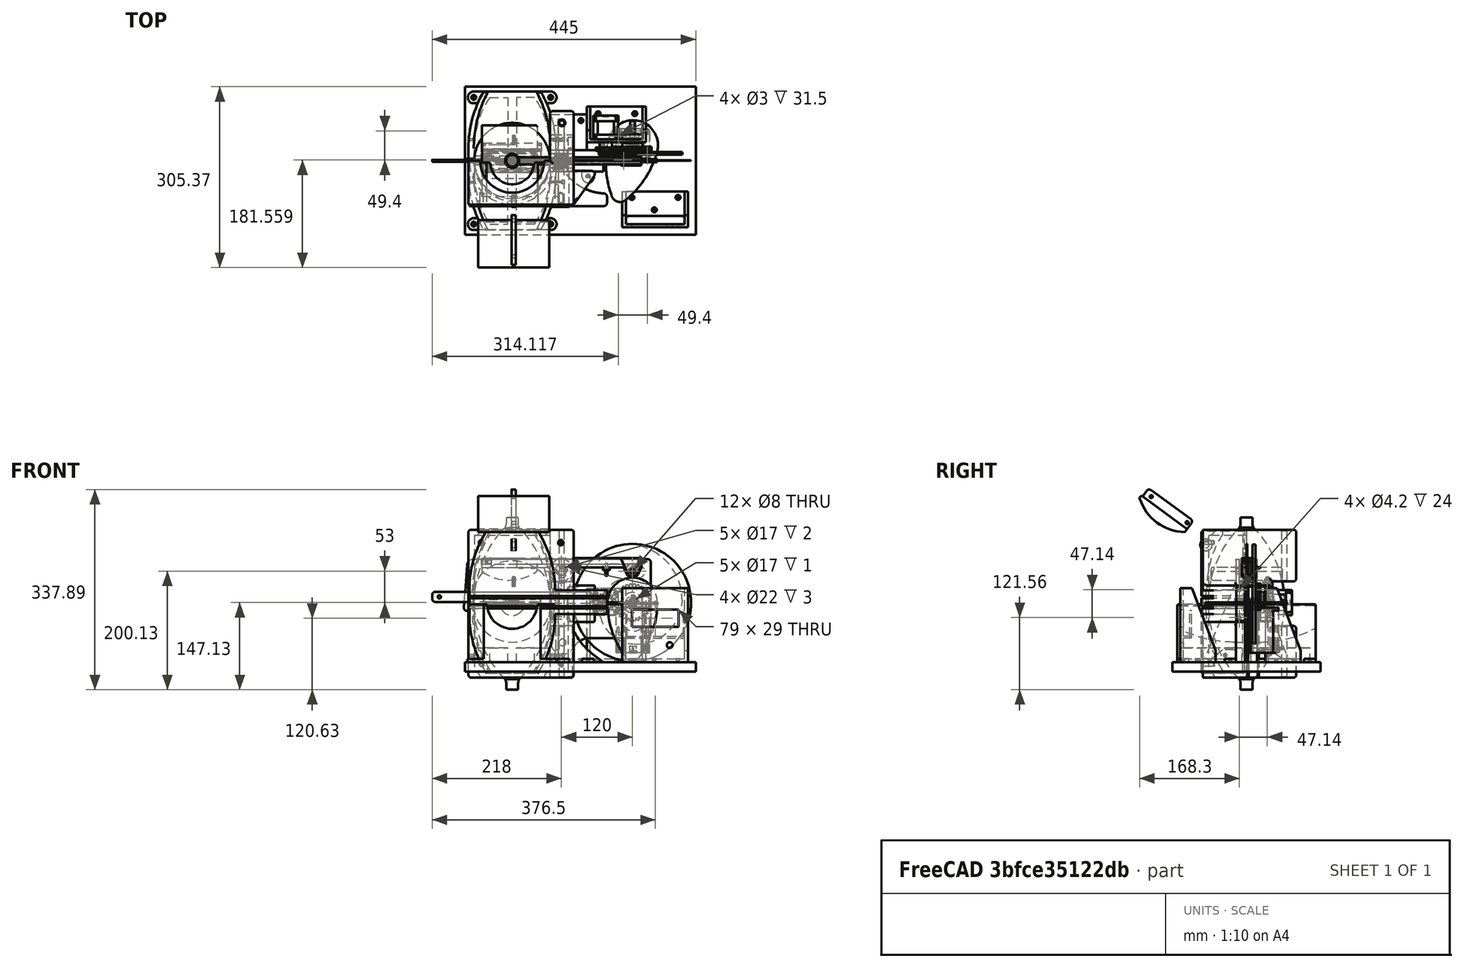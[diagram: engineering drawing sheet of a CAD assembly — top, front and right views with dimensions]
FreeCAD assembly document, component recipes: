
FREECAD ASSEMBLY — COMPONENT RECIPES ("respirador23.0.1")

This assembly document has 5 components, labeled P0..P4 below (a component is one placed body or linked part). 0 of them carry a construction recipe — the FreeCAD feature program that regenerates the part from scratch, quoted from this document or its linked companion documents; the rest are supplied as boundary geometry only. No exploded tour is included for this assembly.
COMPONENT P0 — geometry summary ("palanca-CNC-LASER001"; no construction recipe available for this part):
  bounding box: 224.6 x 170.7 x 13.0 mm
  tessellated surface: 5,376 triangles
  volume: 33917 mm^3 (7% of its bounding box)
  symmetry: mirror-symmetric across its x mid-plane
COMPONENT P1 — geometry summary ("AR M006"; no construction recipe available for this part):
  bounding box: 205.9 x 153.8 x 15.0 mm
  tessellated surface: 5,520 triangles
  volume: 353 mm^3 (0% of its bounding box)
COMPONENT P2 — geometry summary ("item_8_0_004_12_biq41gv2ypkypls4gfckj5y0b001"; no construction recipe available for this part):
  bounding box: 204.4 x 152.3 x 26.0 mm
  tessellated surface: 8,754 triangles
  volume: 1916 mm^3 (0% of its bounding box)
COMPONENT P3 — geometry summary ("tuerca_din934_m5-011"; no construction recipe available for this part):
  bounding box: 205.0 x 152.8 x 9.0 mm
  tessellated surface: 11,080 triangles
  volume: 813 mm^3 (0% of its bounding box)
COMPONENT P4 — geometry summary ("Pieza016"; no construction recipe available for this part):
  bounding box: 315.4 x 160.4 x 19.0 mm
  tessellated surface: 7,864 triangles
  volume: 147992 mm^3 (15% of its bounding box)
  symmetry: mirror-symmetric across its z mid-plane
PROVENANCE & LICENSES
A FreeCAD (.FCStd) document from a public repository crawl; recipes are the document's own serialized feature recipes (and, for linked parts, companion documents' recipes).
License: mit.
